# Revit family: SH-7450
name_source: partatom
category: Lighting Fixtures
revit_build: Autodesk Revit 2017 (Build: 20160225_1515(x64)
units: mm (PartAtom-declared; Revit-internal decimal feet)

## family parameters
Cut with Voids When Loaded = No
Host = Face
Light Source = Yes
Part Type = Normal
Room Calculation Point = No
Round Connector Dimension = Use Diameter
Shared = No

## types (2) — shared parameters
Body Material = Aluminum
Body color = Gray color
Color Filter = 16777215
Default Elevation = 122 cm
Diffuser Material = Glass
Dimming Lamp Color Temperature Shift = <None>
IP = IP65
Lamp = LED
Manufacturer = SHOA
Model = SH-7450
Photometric Web File = 150_IESNA2002(1).IES
Protection Class = Class I
Tilt Angle = 90.00°
Type medule = COB
URL = https://www.shoaco.com
Voltage/Frequency = 230v/50hz
Wattage. = 200 W
Width = 36 cm
color temperature = 3000K-6000K
consumption current = 1 A
website = www.shoaco.com

## per-type parameters (varying)
| type | Length |
| SH-7450(Gray color-3000K-LED) | 97 cm |
| SH-7450(Gray color-6000K-LED) | 95 cm |

## geometry (parser evidence)
native form markers: Sweep x3
no freeform markers — native parametric forms only
